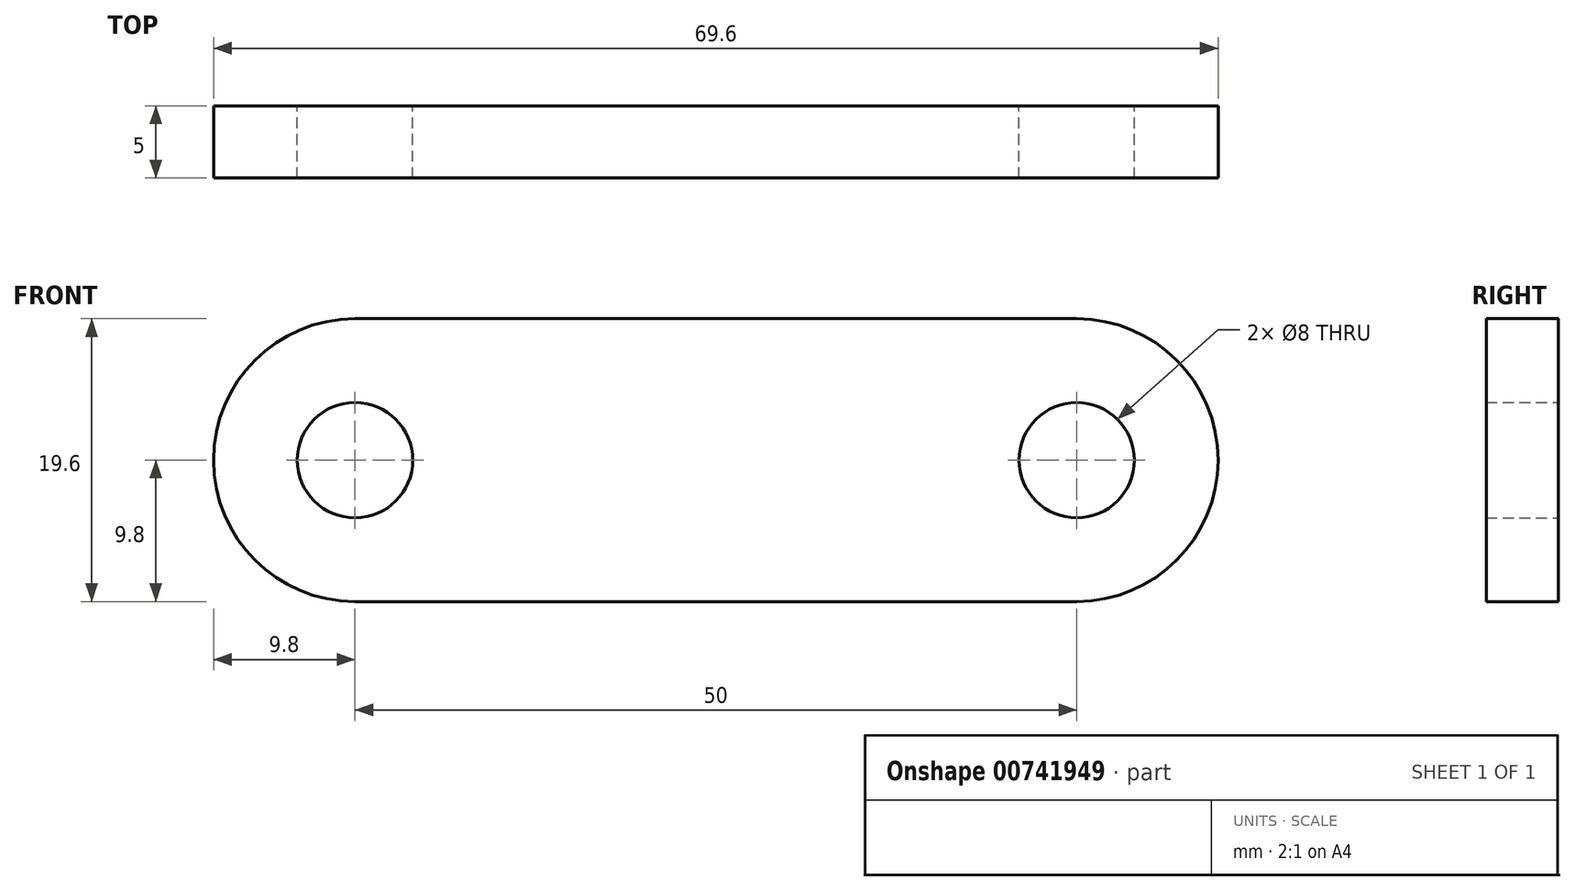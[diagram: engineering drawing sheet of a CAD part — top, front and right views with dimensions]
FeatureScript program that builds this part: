
annotation { "Feature Type Name" : "Feature", "Feature Type Description" : "" }
export const myFeature = defineFeature(function(context is Context, id is Id, definition is map)
    precondition{}
    {
        {
            var Q0;
            Q0=qCreatedBy(makeId("Front.planeOp"),FACE);
            var sketch = newSketch(context, id + "F0", { "sketchPlane" : qUnion([Q0])});
            skLineSegment(sketch, "E0", {"start": v(-50.31, 0) * mm, "end": v(52.82, 0) * mm, "construction": true});
            skLineSegment(sketch, "E1", {"start": v(0, -42.26) * mm, "end": v(0, 45.4) * mm, "construction": true});
            skLineSegment(sketch, "E2", {"start": v(0, 9.8) * mm, "end": v(-25, 9.8) * mm});
            skLineSegment(sketch, "E3.MirrorCS", {"start": v(0, -9.8) * mm, "end": v(-25, -9.8) * mm});
            skArc(sketch, "E4", {"start": v(-25, 9.8) * mm, "mid": v(-34.8, 0) * mm, "end": v(-25, -9.8) * mm});
            skCircle(sketch, "E5", {"center": v(-25, 0) * mm, "radius": 4 * mm});
            skLineSegment(sketch, "E6.MirrorCS", {"start": v(0, 9.8) * mm, "end": v(25, 9.8) * mm});
            skLineSegment(sketch, "E7.MirrorCS", {"start": v(0, -9.8) * mm, "end": v(25, -9.8) * mm});
            skCircle(sketch, "E8.MirrorC", {"center": v(25, 0) * mm, "radius": 4 * mm});
            skArc(sketch, "E9.MirrorCS", {"start": v(25, 9.8) * mm, "mid": v(34.8, 0) * mm, "end": v(25, -9.8) * mm});
            skSolve(sketch);
        }
        {
            var Q0;
            Q0 = qSketchRegion(id + "F0", true);
            extrude(context, id + "F1", {"entities" : qUnion([Q0]), "endBound" : BoundingType.SYMMETRIC, "depth" : 5 * mm, "offsetDistance" : 25.4 * mm});
        }
    });
